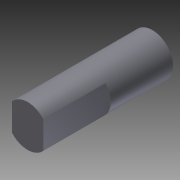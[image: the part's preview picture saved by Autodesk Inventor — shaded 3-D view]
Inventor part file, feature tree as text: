
AUTODESK INVENTOR PART (.ipt)
format: ipt  version: 2012 (Build 160160000, 160)  size: 83,456 bytes
history: native  units: in
note: dims shown in document units (in); Inventor stores cm internally (conversion verified against a paired STEP export)
features: extrude x2, sketch x2
ambient origin geometry x8: Origin, YZ Plane, XZ Plane, XY Plane, X Axis, Y Axis, Z Axis, Center Point
bodies: Solid1 (feature_tree)
feature tree (4):
  extrude  "Extrusion1"  Depth=1.5in TaperAngle=0.0deg
  extrude  "Extrusion2"  Depth=0.75in TaperAngle=0.0deg
  sketch  "Sketch1"  dims[d0=0.5in d1=1.5in d2=0.0in]
  sketch  "Sketch2"  dims[d3=0.1875in d4=0.75in d5=0.0in]
